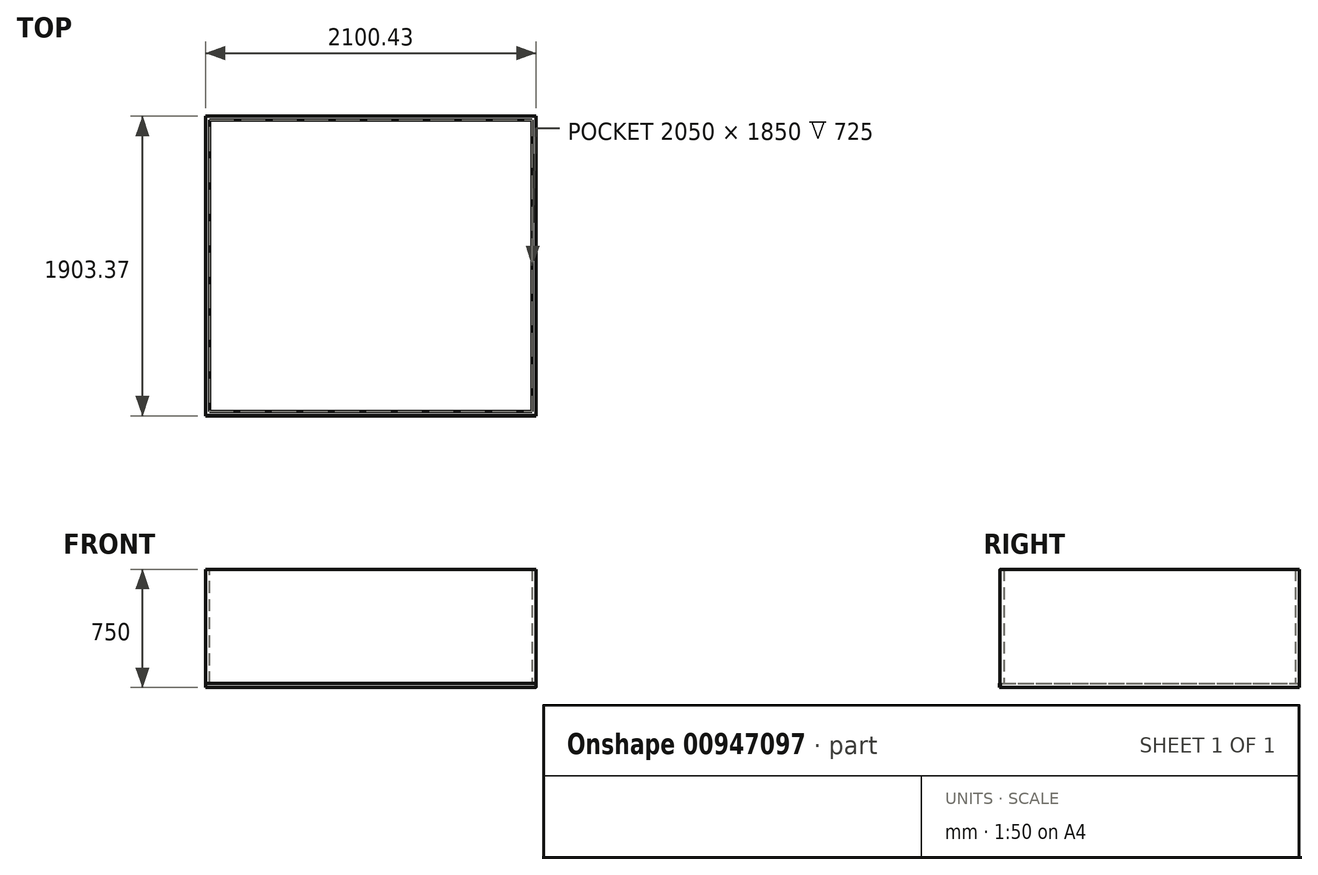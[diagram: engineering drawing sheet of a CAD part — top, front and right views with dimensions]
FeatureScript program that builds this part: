
annotation { "Feature Type Name" : "Feature", "Feature Type Description" : "" }
export const myFeature = defineFeature(function(context is Context, id is Id, definition is map)
    precondition{}
    {
        {
            var Q0;
            Q0=qCreatedBy(makeId("Top.planeOp"),FACE);
            var sketch = newSketch(context, id + "F0", { "sketchPlane" : qUnion([Q0])});
            skLineSegment(sketch, "E0.bottom", {"start": v(-1049.74, 832.38) * mm, "end": v(1050.26, 832.38) * mm});
            skLineSegment(sketch, "E0.top", {"start": v(-1049.74, -1067.62) * mm, "end": v(1050.26, -1067.62) * mm});
            skLineSegment(sketch, "E0.left", {"start": v(-1049.74, 832.38) * mm, "end": v(-1049.74, -1067.62) * mm});
            skLineSegment(sketch, "E0.right", {"start": v(1050.26, 832.38) * mm, "end": v(1050.26, -1067.62) * mm});
            skSolve(sketch);
        }
        {
            var Q0;
            Q0=sQuery(id+"F0.wireOp",EDGE,"E0.bottom");
            var Q1;
            Q1=sQuery(id+"F0.wireOp",EDGE,"E0.right");
            var Q2;
            Q2=sQuery(id+"F0.wireOp",EDGE,"E0.left");
            var Q3;
            Q3=sQuery(id+"F0.wireOp",EDGE,"E0.top");
            extrude(context, id + "F1", {"bodyType" : ToolBodyType.SURFACE, "surfaceEntities" : qUnion([Q0, Q1, Q2, Q3]), "depth" : 750 * mm, "offsetDistance" : 25 * mm});
        }
        {
            var Q0;
            Q0=makeQuery(id+"F1.opExtrude","SWEPT_FACE",FACE,{"disambiguationData":[OSD([sQuery(id+"F0.wireOp",EDGE,"E0.bottom")])]});
            extrude(context, id + "F2", {"entities" : qUnion([Q0]), "depth" : 25 * mm, "offsetDistance" : 25 * mm});
        }
        {
            var Q0;
            Q0=makeQuery(id+"F1.opExtrude","SWEPT_FACE",FACE,{"disambiguationData":[OSD([sQuery(id+"F0.wireOp",EDGE,"E0.right")])]});
            extrude(context, id + "F3", {"entities" : qUnion([Q0]), "operationType" : NewBodyOperationType.ADD, "depth" : 25 * mm, "offsetDistance" : 25 * mm});
        }
        {
            var Q0;
            Q0=makeQuery(id+"F1.opExtrude","SWEPT_FACE",FACE,{"disambiguationData":[OSD([sQuery(id+"F0.wireOp",EDGE,"E0.top")])]});
            extrude(context, id + "F4", {"entities" : qUnion([Q0]), "operationType" : NewBodyOperationType.ADD, "depth" : 25 * mm, "offsetDistance" : 25 * mm});
        }
        {
            var Q0;
            Q0=makeQuery(id+"F1.opExtrude","SWEPT_FACE",FACE,{"disambiguationData":[OSD([sQuery(id+"F0.wireOp",EDGE,"E0.left")])]});
            extrude(context, id + "F5", {"entities" : qUnion([Q0]), "operationType" : NewBodyOperationType.ADD, "depth" : 25 * mm, "offsetDistance" : 25 * mm});
        }
        {
            var Q0;
            Q0=qCreatedBy(makeId("Top.planeOp"),FACE);
            var sketch = newSketch(context, id + "F6", { "sketchPlane" : qUnion([Q0])});
            skLineSegment(sketch, "E1.bottom", {"start": v(-1050.17, -1071) * mm, "end": v(1049.83, -1071) * mm});
            skLineSegment(sketch, "E1.top", {"start": v(-1050.17, 829) * mm, "end": v(1049.83, 829) * mm});
            skLineSegment(sketch, "E1.left", {"start": v(-1050.17, -1071) * mm, "end": v(-1050.17, 829) * mm});
            skLineSegment(sketch, "E1.right", {"start": v(1049.83, -1071) * mm, "end": v(1049.83, 829) * mm});
            skSolve(sketch);
        }
        {
            var Q0;
            Q0=qSketchRegion(id+"F6",true);
            extrude(context, id + "F7", {"entities" : qUnion([Q0]), "operationType" : NewBodyOperationType.ADD, "depth" : 25 * mm, "offsetDistance" : 25 * mm});
        }
        {
            var Q0;
            Q0=makeQuery(id+"F1.opExtrude","SWEPT_EDGE",EDGE,{"disambiguationData":[OSD([sQuery(id+"F0.wireOp",VERTEX,"E0.top.start")])]});
            var Q1;
            Q1=makeQuery(id+"F1.opExtrude","SWEPT_EDGE",EDGE,{"disambiguationData":[OSD([sQuery(id+"F0.wireOp",VERTEX,"E0.top.end")])]});
            var Q2;
            Q2=makeQuery(id+"F1.opExtrude","SWEPT_EDGE",EDGE,{"disambiguationData":[OSD([sQuery(id+"F0.wireOp",VERTEX,"E0.right.start")])]});
            var Q3;
            Q3=makeQuery(id+"F1.opExtrude","SWEPT_EDGE",EDGE,{"disambiguationData":[OSD([sQuery(id+"F0.wireOp",VERTEX,"E0.left.start")])]});
            fillet(context, id + "F8", {"entities" : qUnion([Q0, Q1, Q2, Q3]), "radius" : 20 * mm, "tangentPropagation" : true, "allowEdgeOverflow" : false});
        }
        {
            var Q0;
            Q0=makeQuery(id+"F3.opExtrude","CAP_EDGE",EDGE,{"disambiguationData":[OSD([sQuery(id+"F0.wireOp",VERTEX,"E0.top.end")])],"isStart":true});
            fillet(context, id + "F9", {"entities" : qUnion([Q0]), "radius" : 5 * mm, "tangentPropagation" : true, "allowEdgeOverflow" : false});
        }
    });
